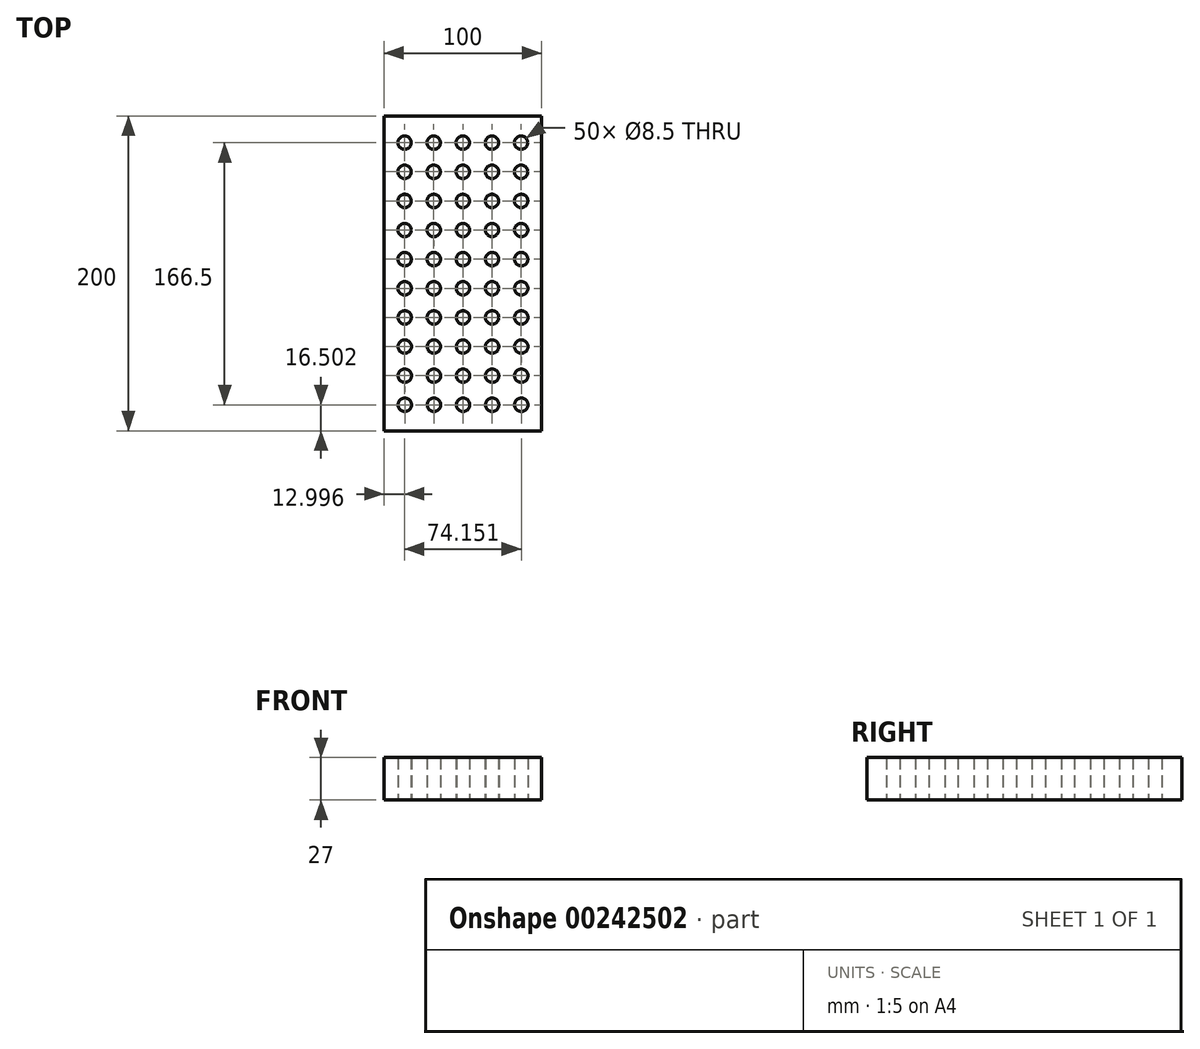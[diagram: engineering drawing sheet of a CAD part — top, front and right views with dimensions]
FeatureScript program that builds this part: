
annotation { "Feature Type Name" : "Feature", "Feature Type Description" : "" }
export const myFeature = defineFeature(function(context is Context, id is Id, definition is map)
    precondition{}
    {
        {
            var Q0;
            Q0=qCreatedBy(makeId("Top.planeOp"),FACE);
            var sketch = newSketch(context, id + "F0", { "sketchPlane" : qUnion([Q0])});
            skLineSegment(sketch, "E0.bottom", {"start": v(-502.31, 47.18) * mm, "end": v(-402.31, 47.18) * mm});
            skLineSegment(sketch, "E0.top", {"start": v(-502.31, 247.18) * mm, "end": v(-402.31, 247.18) * mm});
            skLineSegment(sketch, "E0.left", {"start": v(-502.31, 47.18) * mm, "end": v(-502.31, 247.18) * mm});
            skLineSegment(sketch, "E0.right", {"start": v(-402.31, 47.18) * mm, "end": v(-402.31, 247.18) * mm});
            skLineSegment(sketch, "E1", {"start": v(-502.31, 247.18) * mm, "end": v(-489.31, 247.18) * mm, "construction": true});
            skLineSegment(sketch, "E2", {"start": v(-489.31, 247.18) * mm, "end": v(-489.31, 230.18) * mm, "construction": true});
            skCircle(sketch, "E3", {"center": v(-489.31, 230.18) * mm, "radius": 4.25 * mm});
            skCircle(sketch, "E4.1.0.0", {"center": v(-470.81, 230.18) * mm, "radius": 4.25 * mm});
            skCircle(sketch, "E4.2.0.0", {"center": v(-452.31, 230.18) * mm, "radius": 4.25 * mm});
            skCircle(sketch, "E4.3.0.0", {"center": v(-433.81, 230.18) * mm, "radius": 4.25 * mm});
            skLineSegment(sketch, "E4.direction1", {"start": v(-489.31, 230.18) * mm, "end": v(-470.81, 230.18) * mm, "construction": true});
            skCircle(sketch, "E5.1.0.0", {"center": v(-489.3, 211.68) * mm, "radius": 4.25 * mm});
            skCircle(sketch, "E5.2.0.0", {"center": v(-489.28, 193.18) * mm, "radius": 4.25 * mm});
            skCircle(sketch, "E5.3.0.0", {"center": v(-489.26, 174.68) * mm, "radius": 4.25 * mm});
            skCircle(sketch, "E5.4.0.0", {"center": v(-489.25, 156.18) * mm, "radius": 4.25 * mm});
            skLineSegment(sketch, "E5.direction1", {"start": v(-489.31, 230.18) * mm, "end": v(-489.3, 211.68) * mm, "construction": true});
            skCircle(sketch, "E6.1.0.0", {"center": v(-470.8, 211.68) * mm, "radius": 4.25 * mm});
            skCircle(sketch, "E6.2.0.0", {"center": v(-452.3, 211.68) * mm, "radius": 4.25 * mm});
            skCircle(sketch, "E6.3.0.0", {"center": v(-433.8, 211.68) * mm, "radius": 4.25 * mm});
            skLineSegment(sketch, "E6.direction1", {"start": v(-489.3, 211.68) * mm, "end": v(-470.8, 211.68) * mm, "construction": true});
            skCircle(sketch, "E7.1.0.0", {"center": v(-470.78, 193.18) * mm, "radius": 4.25 * mm});
            skCircle(sketch, "E7.2.0.0", {"center": v(-452.28, 193.18) * mm, "radius": 4.25 * mm});
            skCircle(sketch, "E7.3.0.0", {"center": v(-433.78, 193.18) * mm, "radius": 4.25 * mm});
            skLineSegment(sketch, "E7.direction1", {"start": v(-489.28, 193.18) * mm, "end": v(-470.78, 193.18) * mm, "construction": true});
            skLineSegment(sketch, "E8.direction1", {"start": v(-489.26, 174.68) * mm, "end": v(-470.76, 174.68) * mm, "construction": true});
            skLineSegment(sketch, "E9", {"start": v(-452.31, 247.18) * mm, "end": v(-452.31, 47.18) * mm, "construction": true});
            skLineSegment(sketch, "E10", {"start": v(-502.31, 147.18) * mm, "end": v(-402.31, 147.18) * mm, "construction": true});
            skLineSegment(sketch, "E11.MirrorCS", {"start": v(-402.31, 147.18) * mm, "end": v(-502.31, 147.18) * mm, "construction": true});
            skCircle(sketch, "E12.0.5.0", {"center": v(-489.23, 137.68) * mm, "radius": 4.25 * mm});
            skCircle(sketch, "E12.0.6.0", {"center": v(-489.21, 119.18) * mm, "radius": 4.25 * mm});
            skCircle(sketch, "E12.0.7.0", {"center": v(-489.2, 100.68) * mm, "radius": 4.25 * mm});
            skCircle(sketch, "E12.0.8.0", {"center": v(-489.18, 82.18) * mm, "radius": 4.25 * mm});
            skCircle(sketch, "E12.0.9.0", {"center": v(-489.16, 63.68) * mm, "radius": 4.25 * mm});
            skCircle(sketch, "E13.1.0.0", {"center": v(-470.75, 156.18) * mm, "radius": 4.25 * mm});
            skCircle(sketch, "E13.2.0.0", {"center": v(-452.25, 156.18) * mm, "radius": 4.25 * mm});
            skCircle(sketch, "E13.3.0.0", {"center": v(-433.75, 156.18) * mm, "radius": 4.25 * mm});
            skLineSegment(sketch, "E13.direction1", {"start": v(-489.25, 156.18) * mm, "end": v(-470.75, 156.18) * mm, "construction": true});
            skCircle(sketch, "E14.1.0.0", {"center": v(-470.73, 137.68) * mm, "radius": 4.25 * mm});
            skCircle(sketch, "E14.1.0.1", {"center": v(-470.71, 119.18) * mm, "radius": 4.25 * mm});
            skCircle(sketch, "E14.1.0.2", {"center": v(-470.7, 100.68) * mm, "radius": 4.25 * mm});
            skCircle(sketch, "E14.1.0.3", {"center": v(-470.68, 82.18) * mm, "radius": 4.25 * mm});
            skCircle(sketch, "E14.1.0.4", {"center": v(-470.66, 63.68) * mm, "radius": 4.25 * mm});
            skCircle(sketch, "E14.2.0.0", {"center": v(-452.23, 137.68) * mm, "radius": 4.25 * mm});
            skCircle(sketch, "E14.2.0.1", {"center": v(-452.21, 119.18) * mm, "radius": 4.25 * mm});
            skCircle(sketch, "E14.2.0.2", {"center": v(-452.2, 100.68) * mm, "radius": 4.25 * mm});
            skCircle(sketch, "E14.2.0.3", {"center": v(-452.18, 82.18) * mm, "radius": 4.25 * mm});
            skCircle(sketch, "E14.2.0.4", {"center": v(-452.16, 63.68) * mm, "radius": 4.25 * mm});
            skCircle(sketch, "E14.3.0.0", {"center": v(-433.73, 137.68) * mm, "radius": 4.25 * mm});
            skCircle(sketch, "E14.3.0.1", {"center": v(-433.71, 119.18) * mm, "radius": 4.25 * mm});
            skCircle(sketch, "E14.3.0.2", {"center": v(-433.7, 100.68) * mm, "radius": 4.25 * mm});
            skCircle(sketch, "E14.3.0.3", {"center": v(-433.68, 82.18) * mm, "radius": 4.25 * mm});
            skCircle(sketch, "E14.3.0.4", {"center": v(-433.66, 63.68) * mm, "radius": 4.25 * mm});
            skLineSegment(sketch, "E14.direction1", {"start": v(-489.23, 137.68) * mm, "end": v(-470.73, 137.68) * mm, "construction": true});
            skCircle(sketch, "E15.1.0.0", {"center": v(-470.76, 174.68) * mm, "radius": 4.25 * mm});
            skCircle(sketch, "E15.2.0.0", {"center": v(-452.26, 174.68) * mm, "radius": 4.25 * mm});
            skCircle(sketch, "E15.3.0.0", {"center": v(-433.76, 174.68) * mm, "radius": 4.25 * mm});
            skCircle(sketch, "E16.0.4.0", {"center": v(-415.23, 137.68) * mm, "radius": 4.25 * mm});
            skCircle(sketch, "E16.2.4.0", {"center": v(-415.21, 119.18) * mm, "radius": 4.25 * mm});
            skCircle(sketch, "E16.4.4.0", {"center": v(-415.2, 100.68) * mm, "radius": 4.25 * mm});
            skCircle(sketch, "E16.6.4.0", {"center": v(-415.18, 82.18) * mm, "radius": 4.25 * mm});
            skCircle(sketch, "E16.8.4.0", {"center": v(-415.16, 63.68) * mm, "radius": 4.25 * mm});
            skCircle(sketch, "E17.0.4.0", {"center": v(-415.25, 156.18) * mm, "radius": 4.25 * mm});
            skCircle(sketch, "E18.0.4.0", {"center": v(-415.28, 193.18) * mm, "radius": 4.25 * mm});
            skCircle(sketch, "E19.0.4.0", {"center": v(-415.31, 230.18) * mm, "radius": 4.25 * mm});
            skCircle(sketch, "E20.0.4.0", {"center": v(-415.26, 174.68) * mm, "radius": 4.25 * mm});
            skCircle(sketch, "E21.0.4.0", {"center": v(-415.3, 211.68) * mm, "radius": 4.25 * mm});
            skSolve(sketch);
        }
        {
            var Q0;
            Q0 = qSketchRegion(id + "F0", true);
            extrude(context, id + "F1", {"entities" : qUnion([Q0]), "depth" : 27 * mm});
        }
    });
